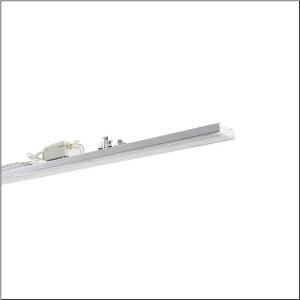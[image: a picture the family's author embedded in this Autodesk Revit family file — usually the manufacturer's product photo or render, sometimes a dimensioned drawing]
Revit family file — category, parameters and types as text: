
# Revit family: licross_r__21_recessed_mo_52te14dv4exg_6364
name_source: partatom
category: Lighting Fixtures
units: mm (PartAtom-declared; Revit-internal decimal feet)

## family parameters
Cut with Voids When Loaded = No
Host = Face
Light Source = No
Part Type = Normal
Room Calculation Point = No
Round Connector Dimension = Use Diameter
Shared = No

## types (1)
- --- (1 x LED, 14200 lm, 85.3 W, 4000K)
    Apparent Load = 85 VA
    CIE Flux Codes = 56 84 97 100 100
    Color Rendering = 80
    Color Temperature = 4000K
    Default Elevation = 1800 mm
    Description = Licross® 21 Recessed MO, luminaire insert, of sheet steel, galvanised, coil coated, white, length: 2.250mm, width: 66mm, height: 67mm, LED rated luminous flux: 14.200lm, light colour: 840, control gear: DALI 2, with plug, 5-pole, with phase selection, mains connection: 220..240V, AC, 50/60Hz, rated input power: 85W, halogen-free wiring, primary light control with lens, of plastic, primary optical cover: cover, of PMMA, light emission: direct distribution, primary light characteristic: asymmetric, protection rating (complete): IP54, insulation class (complete): insulation class I (protective earthing), certification: CE, ENEC, VDE, UKCA, protection symbol: D if used in an environment with non-conductive dust loads with corresponding accessories, impact resistance: IK06, permissible ambient temperature for indoor applications: -25..+35°C, corresponds to IFS (International Featured Standards) requirements for safety and quality in the food industry, reducing of maximum allowable ambient temperature of 5°C with ceiling mounting, LABS conformity tested according to VDMA 24364:2018-05, packaging unit: 1 piece
    Height = 58 mm
    Lamp = 1 x LED
    Lamp Light Flux = 14200 lm
    Lamp Power = 85.3 W
    Lamp count = 1
    Length = 2250 mm
    Luminous efficacy = 166 lm/W
    Manufacturer = Siteco
    ModVariant = No
    Model = 52TE14DV4EXG
    Mounting Place = Ceiling
    Mounting Type = Pendant
    Number of Poles = 1
    OnlyDefault = Yes
    Power Factor = 1
    Product Name = Licross® 21 Recessed MO
    Product group = luminaire insert
    ProductGroupID = 901
    Protection Class = Protection class I
    Protection Degree = IP 54
    RLX_Detail_Level = 1
    RLX_Emergency_Light_Flux = 0 lm
    RLX_Emergency_Type = 0
    RLX_Emergency_Type_DB = No
    RlxData = <blob elided: 29793 chars, md5=89d0d468>
    Socket = socket
    Standby Power = 0 W
    System Light Flux = 14200 lm
    System Power = 85 W
    Type Comments = factory setting: luminous flux: 100 % | dim-lin: 254 | 390 mA
    Type Image = l_1296930.jpg
    URL = http://relux.com
    VarID = @adj_059411
    Voltage = 0 V
    Weight = 0.00 kg
    Width = 66 mm

## geometry (parser evidence)
native form markers: Blend x4, Sweep x11
no freeform markers — native parametric forms only
